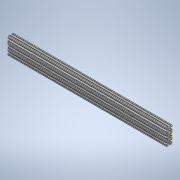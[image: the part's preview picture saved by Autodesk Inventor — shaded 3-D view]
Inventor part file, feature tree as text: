
AUTODESK INVENTOR PART (.ipt)
format: ipt  version: 2020 (Build 240168000, 168)  size: 380,928 bytes
history: native  units: in
note: dims shown in document units (in); Inventor stores cm internally (conversion verified against a paired STEP export)
features: sketch x2, extrude x1
ambient origin geometry x8: Origin, YZ Plane, XZ Plane, XY Plane, X Axis, Y Axis, Z Axis, Center Point
bodies: Solid1 (feature_tree)
feature tree (3):
  extrude  "Extrusion1"  [1 undecoded]
  sketch  "Sketch2"
  sketch  "Sketch1"  dims[d0=28.0in d1=0.0in]
note: 1 required parameter value undecoded (feature->parameter linkage not recoverable at this tier; creation-order binding heuristic only, values carry confidence <= 0.55)
